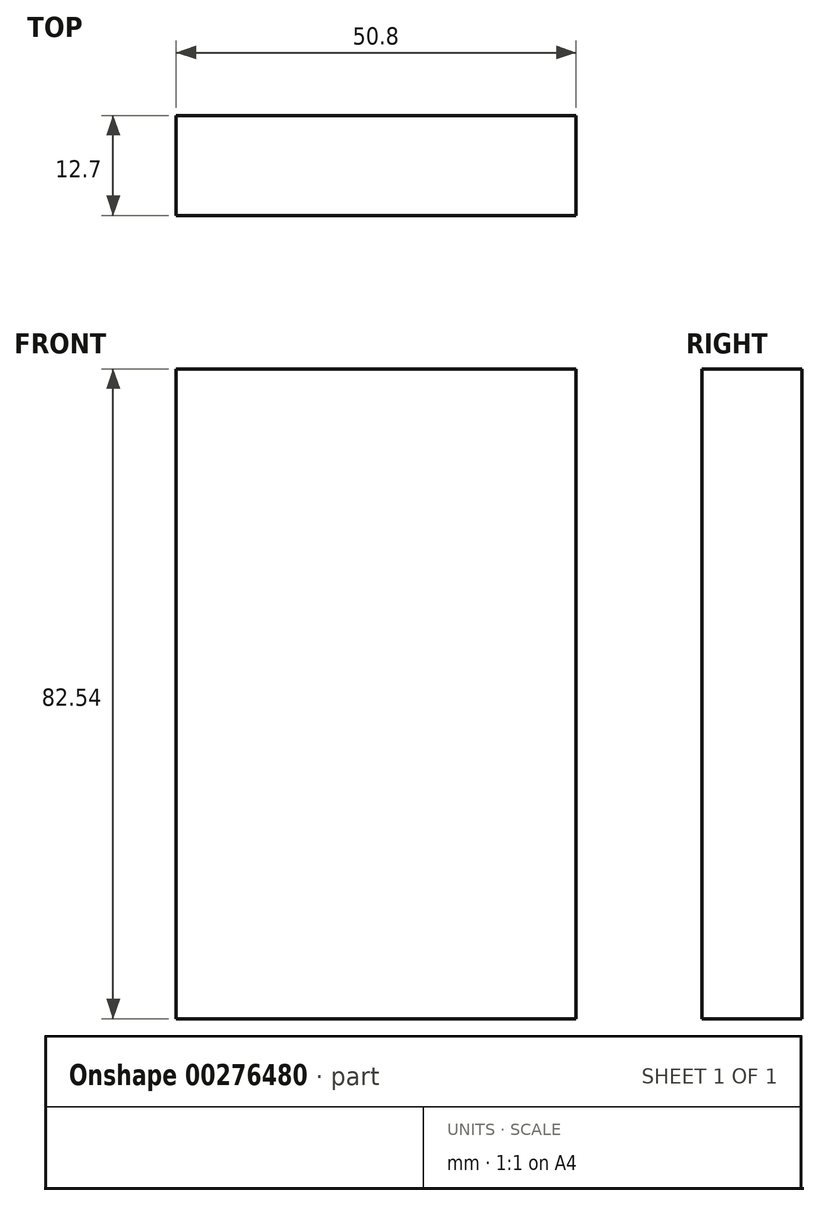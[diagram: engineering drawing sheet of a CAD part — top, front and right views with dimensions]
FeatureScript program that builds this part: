
annotation { "Feature Type Name" : "Feature", "Feature Type Description" : "" }
export const myFeature = defineFeature(function(context is Context, id is Id, definition is map)
    precondition{}
    {
        {
            var Q0;
            Q0=qCreatedBy(makeId("Front.planeOp"),FACE);
            var sketch = newSketch(context, id + "F0", { "sketchPlane" : qUnion([Q0])});
            skLineSegment(sketch, "E0", {"start": v(0, 41.28) * mm, "end": v(50.8, 41.28) * mm});
            skLineSegment(sketch, "E1", {"start": v(50.8, 41.28) * mm, "end": v(50.8, -41.28) * mm});
            skLineSegment(sketch, "E2", {"start": v(50.8, -41.28) * mm, "end": v(0, -41.28) * mm});
            skLineSegment(sketch, "E3", {"start": v(0, -41.28) * mm, "end": v(0, 41.28) * mm});
            skSolve(sketch);
        }
        {
            var Q0;
            Q0=makeQuery(id+"F0.imprint","IMPRINT",FACE,{"disambiguationData":[TD([[makeQuery(id+"F0.imprint","IMPRINT",EDGE,{"derivedFrom":sQuery(id+"F0.wireOp",EDGE,"17ua1O5G-PTPY-SJWb-iF8f-NifK9cDzjIuI")}),-1.0]])]});
            var Q1;
            Q1=makeQuery(id+"F0.imprint","IMPRINT",FACE,{"disambiguationData":[TD([[makeQuery(id+"F0.imprint","IMPRINT",EDGE,{"derivedFrom":sQuery(id+"F0.wireOp",EDGE,"E0")}),-1.0]])]});
            extrude(context, id + "F1", {"entities" : qUnion([Q0, Q1]), "depth" : 12.7 * mm});
        }
    });
